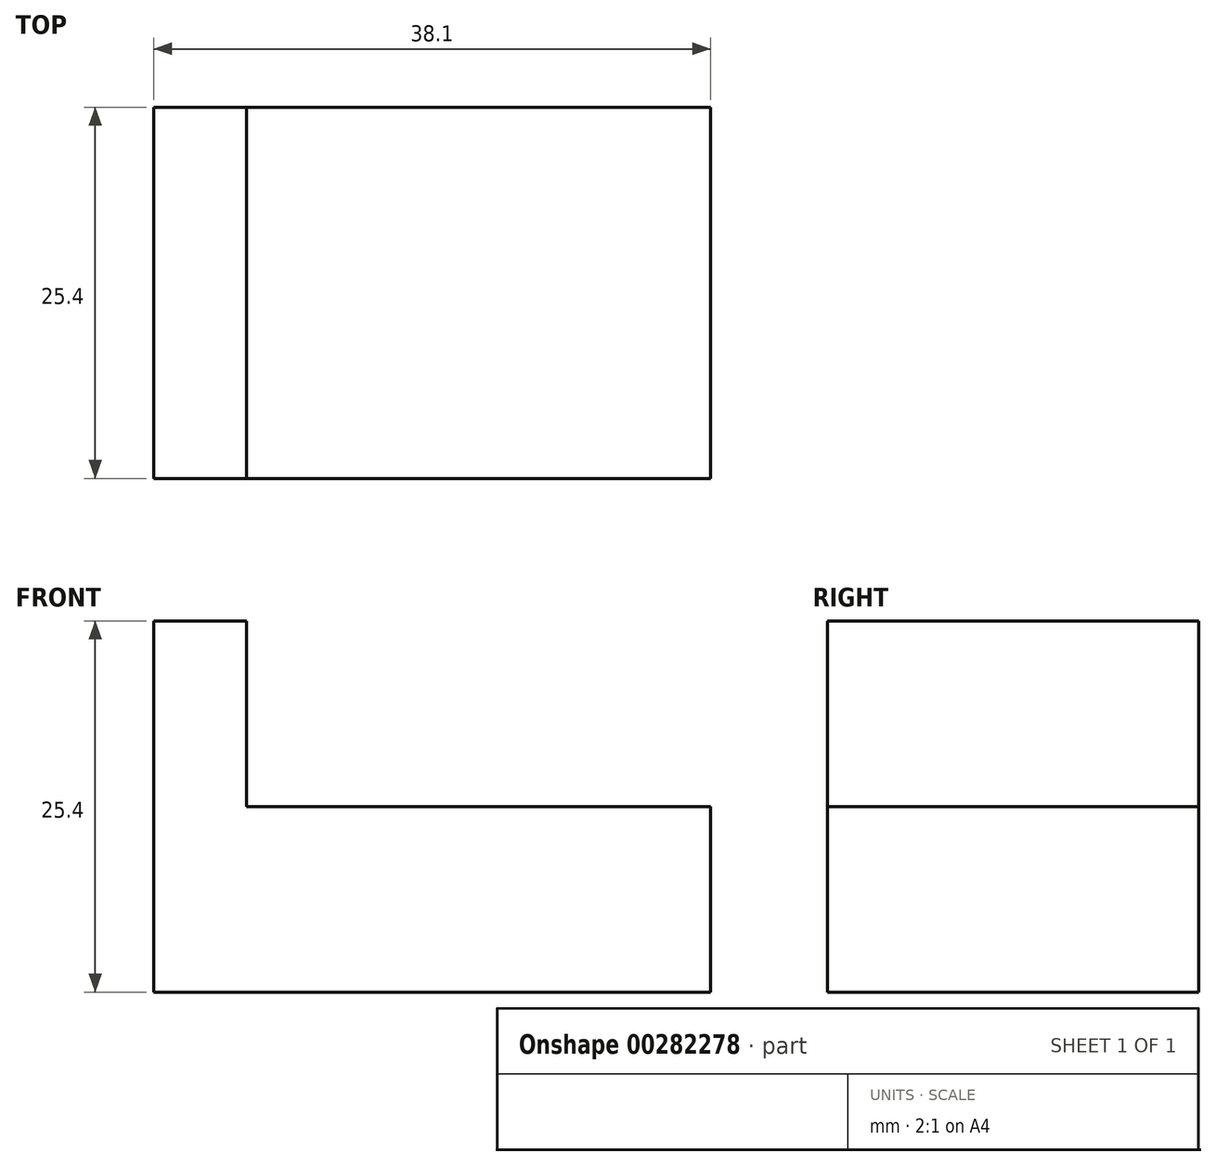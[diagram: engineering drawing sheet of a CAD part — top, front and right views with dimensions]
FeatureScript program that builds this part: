
annotation { "Feature Type Name" : "Feature", "Feature Type Description" : "" }
export const myFeature = defineFeature(function(context is Context, id is Id, definition is map)
    precondition{}
    {
        {
            var Q0;
            Q0=qCreatedBy(makeId("Front.planeOp"),FACE);
            var sketch = newSketch(context, id + "F0", { "sketchPlane" : qUnion([Q0])});
            skLineSegment(sketch, "E0", {"start": v(0, 0) * mm, "end": v(0, 25.4) * mm});
            skLineSegment(sketch, "E1", {"start": v(0, 25.4) * mm, "end": v(6.35, 25.4) * mm});
            skLineSegment(sketch, "E2", {"start": v(6.35, 25.4) * mm, "end": v(6.35, 12.7) * mm});
            skLineSegment(sketch, "E3", {"start": v(6.35, 12.7) * mm, "end": v(38.1, 12.7) * mm});
            skLineSegment(sketch, "E4", {"start": v(38.1, 12.7) * mm, "end": v(38.1, 0) * mm});
            skLineSegment(sketch, "E5", {"start": v(0, 0) * mm, "end": v(38.1, 0) * mm});
            skSolve(sketch);
        }
        {
            var Q0;
            Q0=makeQuery(id+"F0.imprint","IMPRINT",FACE,{"disambiguationData":[TD([[makeQuery(id+"F0.imprint","IMPRINT",EDGE,{"derivedFrom":sQuery(id+"F0.wireOp",EDGE,"E0")}),-1.0]])]});
            extrude(context, id + "F1", {"entities" : qUnion([Q0]), "depth" : 25.4 * mm});
        }
    });
